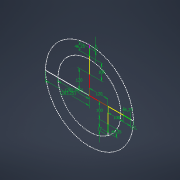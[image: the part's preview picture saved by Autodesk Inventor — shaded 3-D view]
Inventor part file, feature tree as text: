
AUTODESK INVENTOR PART (.ipt)
format: ipt  version: 2021 (Build 250183000, 183)  size: 94,720 bytes
history: native  units: mm
features: sketch x1
ambient origin geometry x8: Origin, YZ Plane, XZ Plane, XY Plane, X Axis, Y Axis, Z Axis, Center Point
feature tree (1):
  sketch  "Boceto1"  dims[d0=120.0mm d1=100.0mm d2=46.25mm d3=120.0mm d4=100.0mm d5=46.25mm d7=100.0mm d8=46.25mm d9=17.0mm d10=17.0mm d11=17.0mm d13=283.25mm d14=202.609384mm]
